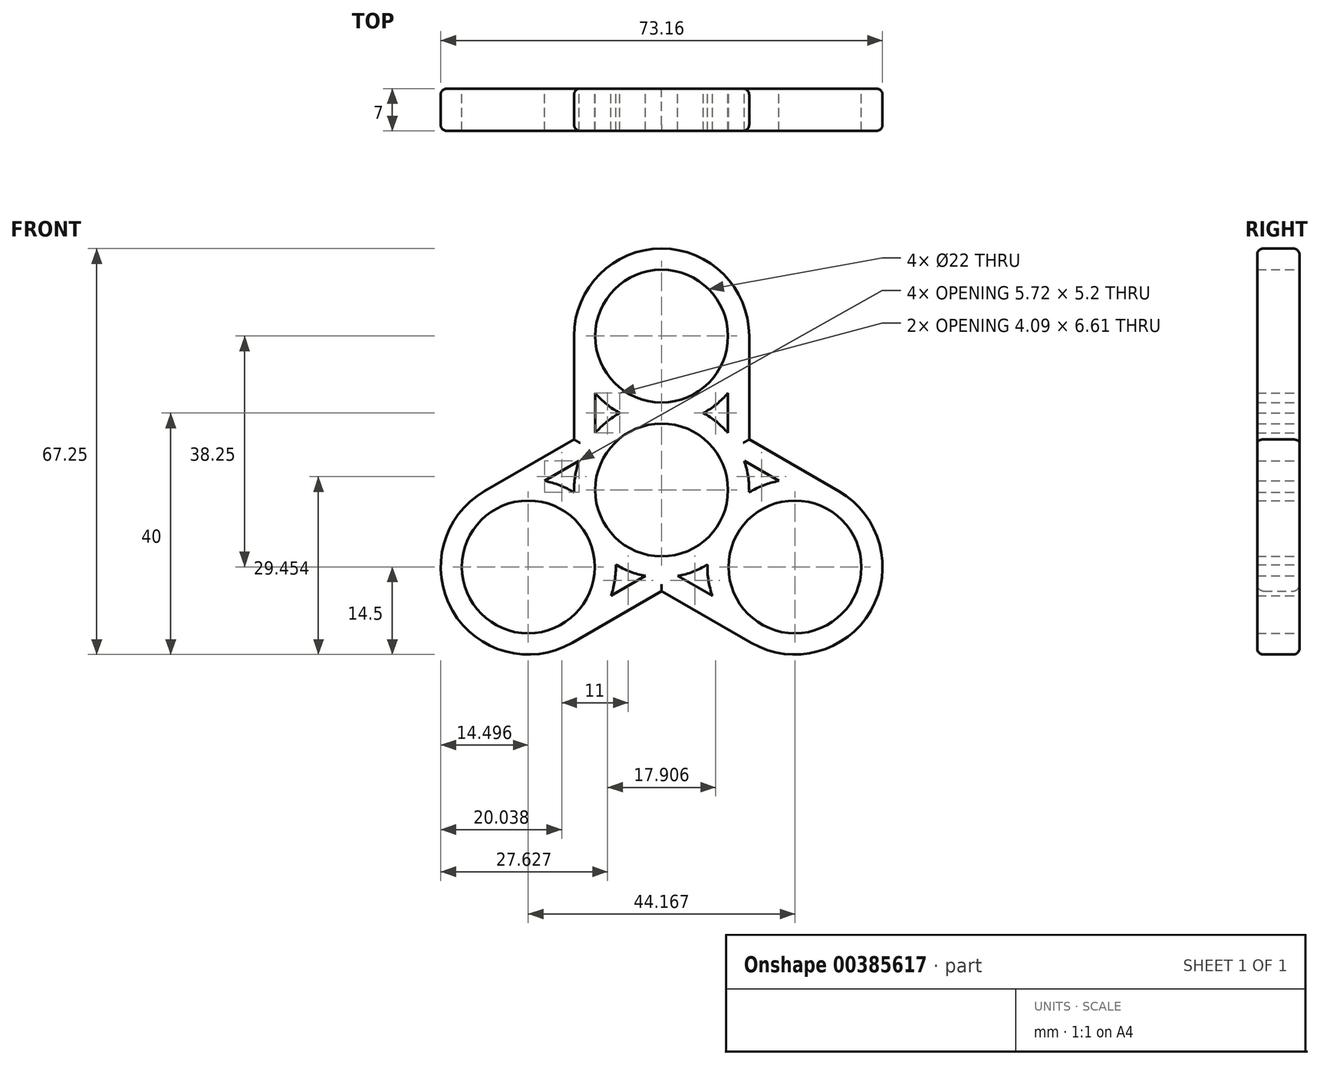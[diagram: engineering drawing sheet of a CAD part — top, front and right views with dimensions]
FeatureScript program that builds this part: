
annotation { "Feature Type Name" : "Feature", "Feature Type Description" : "" }
export const myFeature = defineFeature(function(context is Context, id is Id, definition is map)
    precondition{}
    {
        {
            var Q0;
            Q0=qCreatedBy(makeId("Front.planeOp"),FACE);
            var sketch = newSketch(context, id + "F0", { "sketchPlane" : qUnion([Q0])});
            skCircle(sketch, "E0", {"center": v(0, 0) * mm, "radius": 11 * mm});
            skCircle(sketch, "E1", {"center": v(0, 25.5) * mm, "radius": 11 * mm});
            skArc(sketch, "E2.converted", {"start": v(-11, 16.05) * mm, "mid": v(-9.1, 14.21) * mm, "end": v(-6.9, 12.75) * mm});
            skArc(sketch, "E3.converted", {"start": v(-14.5, 0) * mm, "mid": v(-14.5, -0.2) * mm, "end": v(-14.5, -0.4) * mm});
            skLineSegment(sketch, "E4", {"start": v(-14.5, 25.5) * mm, "end": v(-14.5, 8.37) * mm});
            skLineSegment(sketch, "E5", {"start": v(14.5, 25.5) * mm, "end": v(14.5, 8.37) * mm});
            skLineSegment(sketch, "E6", {"start": v(-11, 16.05) * mm, "end": v(-11, 9.45) * mm});
            skLineSegment(sketch, "E7", {"start": v(11, 16.05) * mm, "end": v(11, 9.45) * mm});
            skPoint(sketch, "E8.orphan", {"position": v(-11, 25.5) * mm});
            skArc(sketch, "E9.trimOffspring", {"start": v(6.9, 12.75) * mm, "mid": v(9.1, 14.21) * mm, "end": v(11, 16.05) * mm});
            skArc(sketch, "E10.trimOffspring", {"start": v(-6.9, 12.75) * mm, "mid": v(-9.1, 11.29) * mm, "end": v(-11, 9.45) * mm});
            skPoint(sketch, "E11.orphan", {"position": v(11, 25.5) * mm});
            skArc(sketch, "E12.trimOffspring", {"start": v(14.5, 25.5) * mm, "mid": v(0, 40) * mm, "end": v(-14.5, 25.5) * mm});
            skPoint(sketch, "E13.orphan", {"position": v(11, 0) * mm});
            skArc(sketch, "E14.trimOffspring", {"start": v(11, 9.45) * mm, "mid": v(9.1, 11.29) * mm, "end": v(6.9, 12.75) * mm});
            skLineSegment(sketch, "E15.1.0", {"start": v(-14.83, -25.3) * mm, "end": v(0, -16.74) * mm});
            skCircle(sketch, "E15.1.1", {"center": v(-22.08, -12.75) * mm, "radius": 11 * mm});
            skArc(sketch, "E15.1.2", {"start": v(-29.33, -0.2) * mm, "mid": v(-34.64, -20) * mm, "end": v(-14.83, -25.3) * mm});
            skLineSegment(sketch, "E15.1.3", {"start": v(-29.33, -0.2) * mm, "end": v(-14.5, 8.37) * mm});
            skArc(sketch, "E15.1.4", {"start": v(-13.68, 4.8) * mm, "mid": v(-14.33, 2.24) * mm, "end": v(-14.5, -0.4) * mm});
            skArc(sketch, "E15.1.5", {"start": v(-14.5, -0.4) * mm, "mid": v(-16.86, 0.78) * mm, "end": v(-19.4, 1.5) * mm});
            skLineSegment(sketch, "E15.1.6", {"start": v(-19.4, 1.5) * mm, "end": v(-13.68, 4.8) * mm});
            skArc(sketch, "E15.1.7", {"start": v(-7.59, -12.36) * mm, "mid": v(-5.22, -13.53) * mm, "end": v(-2.68, -14.25) * mm});
            skLineSegment(sketch, "E15.1.8", {"start": v(-8.4, -17.55) * mm, "end": v(-2.68, -14.25) * mm});
            skArc(sketch, "E15.1.9", {"start": v(-8.4, -17.55) * mm, "mid": v(-7.76, -15) * mm, "end": v(-7.59, -12.36) * mm});
            skLineSegment(sketch, "E15.2.0", {"start": v(29.33, -0.2) * mm, "end": v(14.5, 8.37) * mm});
            skCircle(sketch, "E15.2.1", {"center": v(22.08, -12.75) * mm, "radius": 11 * mm});
            skArc(sketch, "E15.2.2", {"start": v(14.83, -25.3) * mm, "mid": v(34.64, -20) * mm, "end": v(29.33, -0.2) * mm});
            skLineSegment(sketch, "E15.2.3", {"start": v(14.83, -25.3) * mm, "end": v(0, -16.74) * mm});
            skArc(sketch, "E15.2.4", {"start": v(2.68, -14.25) * mm, "mid": v(5.22, -13.53) * mm, "end": v(7.59, -12.36) * mm});
            skArc(sketch, "E15.2.5", {"start": v(7.59, -12.36) * mm, "mid": v(7.76, -15) * mm, "end": v(8.4, -17.55) * mm});
            skLineSegment(sketch, "E15.2.6", {"start": v(8.4, -17.55) * mm, "end": v(2.68, -14.25) * mm});
            skArc(sketch, "E15.2.7", {"start": v(14.5, -0.4) * mm, "mid": v(14.33, 2.24) * mm, "end": v(13.68, 4.8) * mm});
            skLineSegment(sketch, "E15.2.8", {"start": v(19.4, 1.5) * mm, "end": v(13.68, 4.8) * mm});
            skArc(sketch, "E15.2.9", {"start": v(19.4, 1.5) * mm, "mid": v(16.86, 0.78) * mm, "end": v(14.5, -0.4) * mm});
            skArc(sketch, "E16.trimOffspring", {"start": v(14.5, -0.4) * mm, "mid": v(14.5, -0.2) * mm, "end": v(14.5, 0) * mm});
            skSolve(sketch);
        }
        {
            var Q0;
            {var subQ5=sQuery(id+"F0.wireOp",EDGE,"E6");var subQ7=sQuery(id+"F0.wireOp",EDGE,"E1");var subQ8=makeQuery(id+"F0.imprint","INTERSECT",VERTEX,{"derivedFrom":[subQ7,subQ5]});Q0=makeQuery(id+"F0.imprint","IMPRINT",FACE,{"disambiguationData":[TD([[makeQuery(id+"F0.imprint","IMPRINT",EDGE,{"disambiguationData":[TD([[subQ8,1.0]])],"derivedFrom":subQ7}),-1.0]])]});}
            var Q1;
            {var subQ0=sQuery(id+"F0.wireOp",EDGE,"E5");Q1=makeQuery(id+"F0.imprint","IMPRINT",FACE,{"disambiguationData":[TD([[makeQuery(id+"F0.imprint","IMPRINT",EDGE,{"derivedFrom":subQ0}),-1.0]])]});}
            var Q2;
            {var subQ0=sQuery(id+"F0.wireOp",EDGE,"E7");var subQ1=sQuery(id+"F0.wireOp",EDGE,"E1");var subQ2=makeQuery(id+"F0.imprint","INTERSECT",VERTEX,{"derivedFrom":[subQ1,subQ0]});Q2=makeQuery(id+"F0.imprint","IMPRINT",FACE,{"disambiguationData":[TD([[makeQuery(id+"F0.imprint","IMPRINT",EDGE,{"disambiguationData":[TD([[subQ2,1.0]])],"derivedFrom":subQ1}),-1.0]])]});}
            var Q3;
            {var subQ0=sQuery(id+"F0.wireOp",EDGE,"E6");var subQ1=sQuery(id+"F0.wireOp",EDGE,"E1");var subQ2=makeQuery(id+"F0.imprint","INTERSECT",VERTEX,{"derivedFrom":[subQ1,subQ0]});Q3=makeQuery(id+"F0.imprint","IMPRINT",FACE,{"disambiguationData":[TD([[makeQuery(id+"F0.imprint","IMPRINT",EDGE,{"disambiguationData":[TD([[subQ2,-1.0]])],"derivedFrom":subQ1}),-1.0]])]});}
            var Q4;
            {var subQ0=sQuery(id+"F0.wireOp",EDGE,"E2.converted");var subQ1=makeQuery(id+"F0.imprint","INTERSECT",VERTEX,{"derivedFrom":[sQuery(id+"F0.wireOp",EDGE,"E0"),subQ0]});Q4=makeQuery(id+"F0.imprint","IMPRINT",FACE,{"disambiguationData":[TD([[makeQuery(id+"F0.imprint","IMPRINT",EDGE,{"disambiguationData":[TD([[subQ1,1.0]])],"derivedFrom":subQ0}),1.0]])]});}
            var Q5;
            {var subQ0=sQuery(id+"F0.wireOp",EDGE,"E6");var subQ1=sQuery(id+"F0.wireOp",EDGE,"E0");var subQ2=makeQuery(id+"F0.imprint","INTERSECT",VERTEX,{"derivedFrom":[subQ1,subQ0]});Q5=makeQuery(id+"F0.imprint","IMPRINT",FACE,{"disambiguationData":[TD([[makeQuery(id+"F0.imprint","IMPRINT",EDGE,{"disambiguationData":[TD([[subQ2,1.0]])],"derivedFrom":subQ1}),-1.0]])]});}
            var Q6;
            {var subQ0=sQuery(id+"F0.wireOp",EDGE,"E4");Q6=makeQuery(id+"F0.imprint","IMPRINT",FACE,{"disambiguationData":[TD([[makeQuery(id+"F0.imprint","IMPRINT",EDGE,{"derivedFrom":subQ0}),1.0]])]});}
            var Q7;
            {var subQ3=sQuery(id+"F0.wireOp",EDGE,"E6");var subQ7=sQuery(id+"F0.wireOp",EDGE,"E0");var subQ8=makeQuery(id+"F0.imprint","INTERSECT",VERTEX,{"derivedFrom":[subQ7,subQ3]});Q7=makeQuery(id+"F0.imprint","IMPRINT",FACE,{"disambiguationData":[TD([[makeQuery(id+"F0.imprint","IMPRINT",EDGE,{"disambiguationData":[TD([[subQ8,-1.0]])],"derivedFrom":subQ7}),-1.0]])]});}
            var Q8;
            {var subQ0=sQuery(id+"F0.wireOp",EDGE,"E7");var subQ1=sQuery(id+"F0.wireOp",EDGE,"E0");var subQ2=makeQuery(id+"F0.imprint","INTERSECT",VERTEX,{"derivedFrom":[subQ1,subQ0]});Q8=makeQuery(id+"F0.imprint","IMPRINT",FACE,{"disambiguationData":[TD([[makeQuery(id+"F0.imprint","IMPRINT",EDGE,{"disambiguationData":[TD([[subQ2,-1.0]])],"derivedFrom":subQ1}),-1.0]])]});}
            extrude(context, id + "F1", {"entities" : qUnion([Q0, Q1, Q2, Q3, Q4, Q5, Q6, Q7, Q8]), "depth" : 7 * mm, "offsetDistance" : 25 * mm});
        }
        {
            var Q0;
            Q0=makeQuery(id+"F1.opExtrude","CAP_EDGE",EDGE,{"disambiguationData":[OSD([sQuery(id+"F0.wireOp",EDGE,"E15.2.0")])],"isStart":false});
            var Q1;
            Q1=makeQuery(id+"F1.opExtrude","CAP_EDGE",EDGE,{"disambiguationData":[OSD([sQuery(id+"F0.wireOp",EDGE,"E5")])],"isStart":false});
            var Q2;
            Q2=makeQuery(id+"F1.opExtrude","CAP_EDGE",EDGE,{"disambiguationData":[OSD([sQuery(id+"F0.wireOp",EDGE,"E5")])],"isStart":true});
            var Q3;
            Q3=makeQuery(id+"F1.opExtrude","CAP_EDGE",EDGE,{"disambiguationData":[OSD([sQuery(id+"F0.wireOp",EDGE,"E15.2.0")])],"isStart":true});
            var Q4;
            Q4=makeQuery(id+"F1.opExtrude","CAP_EDGE",EDGE,{"disambiguationData":[OSD([sQuery(id+"F0.wireOp",EDGE,"E15.1.0")])],"isStart":false});
            var Q5;
            Q5=makeQuery(id+"F1.opExtrude","CAP_EDGE",EDGE,{"disambiguationData":[OSD([sQuery(id+"F0.wireOp",EDGE,"E15.1.3")])],"isStart":true});
            fillet(context, id + "F2", {"entities" : qUnion([Q0, Q1, Q2, Q3, Q4, Q5]), "radius" : 1 * mm, "tangentPropagation" : true, "allowEdgeOverflow" : false});
        }
    });
